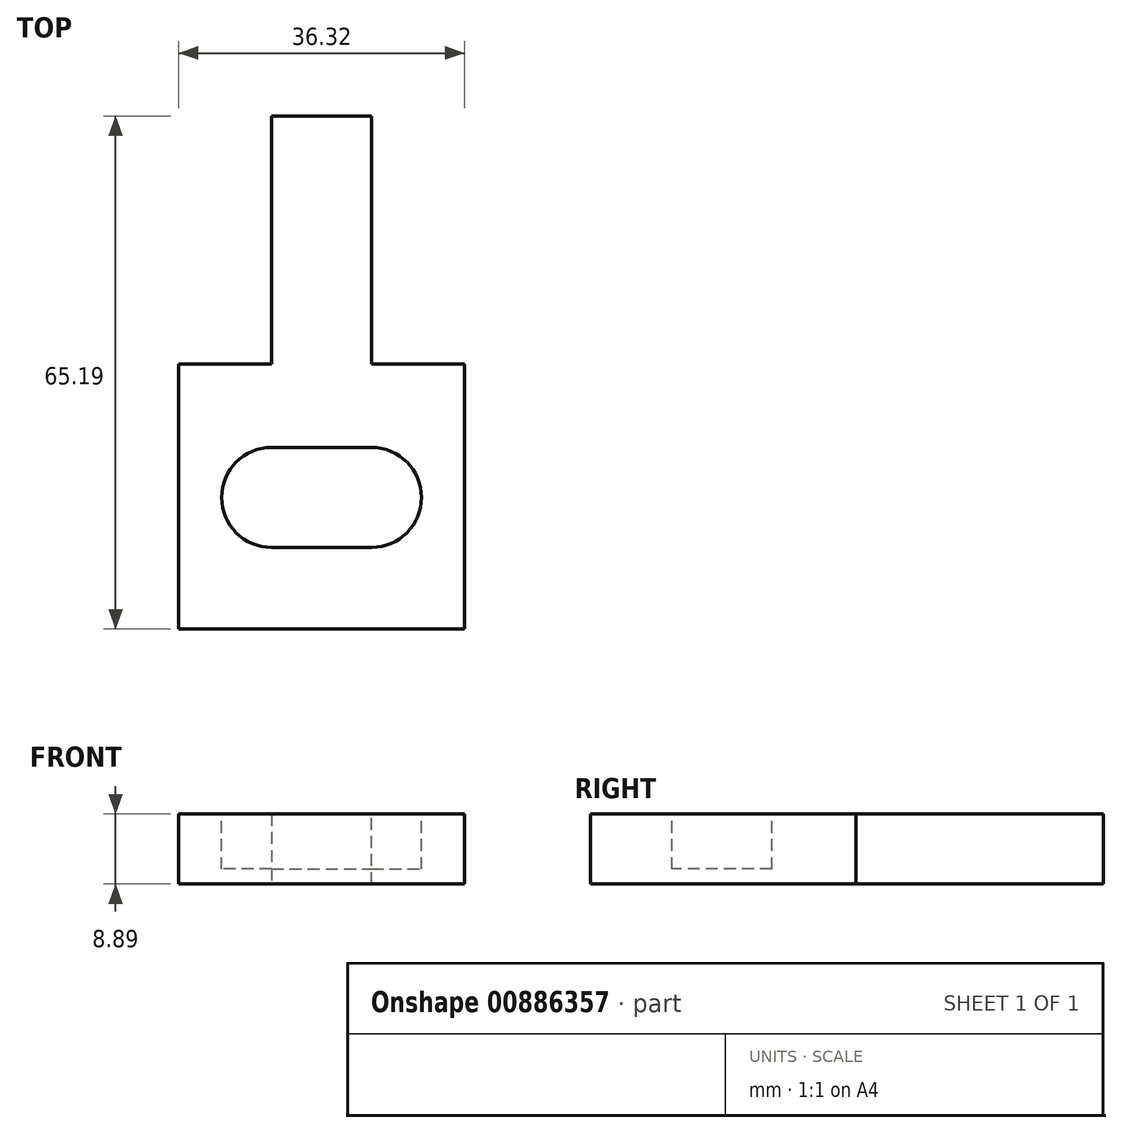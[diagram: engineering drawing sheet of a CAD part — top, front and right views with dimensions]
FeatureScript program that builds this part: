
annotation { "Feature Type Name" : "Feature", "Feature Type Description" : "" }
export const myFeature = defineFeature(function(context is Context, id is Id, definition is map)
    precondition{}
    {
        {
            var Q0;
            Q0=qCreatedBy(makeId("Top.planeOp"),FACE);
            var sketch = newSketch(context, id + "F0", { "sketchPlane" : qUnion([Q0])});
            skLineSegment(sketch, "E0.bottom", {"start": v(0, 0) * mm, "end": v(36.32, 0) * mm});
            skLineSegment(sketch, "E0.top", {"start": v(0, -46.14) * mm, "end": v(36.32, -46.14) * mm});
            skLineSegment(sketch, "E0.left", {"start": v(0, 0) * mm, "end": v(0, -46.14) * mm});
            skLineSegment(sketch, "E0.right", {"start": v(36.32, 0) * mm, "end": v(36.32, -46.14) * mm});
            skSolve(sketch);
        }
        {
            var Q0;
            Q0=makeQuery(id+"F0.imprint","IMPRINT",FACE,{"disambiguationData":[TD([[makeQuery(id+"F0.imprint","IMPRINT",EDGE,{"derivedFrom":sQuery(id+"F0.wireOp",EDGE,"E0.bottom")}),-1.0]])]});
            extrude(context, id + "F1", {"entities" : qUnion([Q0]), "depth" : 8.9 * mm, "offsetDistance" : 25.4 * mm});
        }
        {
            var Q0;
            Q0=makeQuery(id+"F1.opExtrude","CAP_FACE",FACE,{"disambiguationData":[OSD([sQuery(id+"F0.wireOp",EDGE,"E0.bottom"),sQuery(id+"F0.wireOp",EDGE,"E0.top"),sQuery(id+"F0.wireOp",EDGE,"E0.left"),sQuery(id+"F0.wireOp",EDGE,"E0.right")])],"isStart":false});
            var sketch = newSketch(context, id + "F2", { "sketchPlane" : qUnion([Q0])});
            skLineSegment(sketch, "E1", {"start": v(36.32, -46.14) * mm, "end": v(0, -46.14) * mm});
            skLineSegment(sketch, "E2", {"start": v(37, 0) * mm, "end": v(36.32, 0) * mm});
            skArc(sketch, "E3", {"start": v(24.5, -29.42) * mm, "mid": v(30.85, -23.07) * mm, "end": v(24.5, -16.72) * mm});
            skArc(sketch, "E4", {"start": v(11.81, -16.72) * mm, "mid": v(5.47, -23.07) * mm, "end": v(11.81, -29.42) * mm});
            skPoint(sketch, "E5.start.orphan", {"position": v(18.16, -23.07) * mm});
            skLineSegment(sketch, "E6.top", {"start": v(11.81, -29.42) * mm, "end": v(24.5, -29.42) * mm});
            skLineSegment(sketch, "E7.top", {"start": v(11.81, -16.72) * mm, "end": v(24.5, -16.72) * mm});
            skSolve(sketch);
        }
        {
            var Q0;
            Q0=makeQuery(id+"F2.imprint","IMPRINT",FACE,{"disambiguationData":[TD([[makeQuery(id+"F2.imprint","IMPRINT",EDGE,{"derivedFrom":sQuery(id+"F2.wireOp",EDGE,"E3")}),1.0]])]});
            extrude(context, id + "F3", {"entities" : qUnion([Q0]), "operationType" : NewBodyOperationType.REMOVE, "oppositeDirection" : true, "depth" : 7 * mm, "offsetDistance" : 25.4 * mm});
        }
        {
            var Q0;
            Q0=makeQuery(id+"F1.opExtrude","SWEPT_FACE",FACE,{"disambiguationData":[OSD([sQuery(id+"F0.wireOp",EDGE,"E0.bottom")])]});
            var sketch = newSketch(context, id + "F4", { "sketchPlane" : qUnion([Q0])});
            skLineSegment(sketch, "E8", {"start": v(0, 0) * mm, "end": v(0, 8.9) * mm});
            skLineSegment(sketch, "E9.right", {"start": v(-11.82, 4.45) * mm, "end": v(-11.82, 8.9) * mm});
            skLineSegment(sketch, "E10.right", {"start": v(-24.52, 4.45) * mm, "end": v(-24.52, 8.9) * mm});
            skLineSegment(sketch, "E11.top", {"start": v(-24.52, 0) * mm, "end": v(-11.82, 0) * mm});
            skLineSegment(sketch, "E11.left", {"start": v(-24.52, 4.45) * mm, "end": v(-24.52, 0) * mm});
            skLineSegment(sketch, "E11.right", {"start": v(-11.82, 4.45) * mm, "end": v(-11.82, 0) * mm});
            skPoint(sketch, "E12.orphan", {"position": v(-18.16, 4.45) * mm});
            skPoint(sketch, "E13.trimOffspring.end.orphan", {"position": v(-36.32, 0) * mm});
            skLineSegment(sketch, "E14.bottom", {"start": v(-24.52, 8.9) * mm, "end": v(-11.82, 8.9) * mm});
            skLineSegment(sketch, "E14.left", {"start": v(-24.52, 8.9) * mm, "end": v(-24.52, 0) * mm});
            skLineSegment(sketch, "E14.right", {"start": v(-11.82, 8.9) * mm, "end": v(-11.82, 0) * mm});
            skSolve(sketch);
        }
        {
            var Q0;
            Q0=makeQuery(id+"F4.imprint","IMPRINT",FACE,{"disambiguationData":[TD([[makeQuery(id+"F4.imprint","IMPRINT",EDGE,{"derivedFrom":sQuery(id+"F4.wireOp",EDGE,"E14.bottom")}),1.0]])]});
            extrude(context, id + "F5", {"entities" : qUnion([Q0]), "operationType" : NewBodyOperationType.ADD, "depth" : 25.4 * mm, "offsetDistance" : 25.4 * mm});
        }
        {
            var Q0;
            Q0=makeQuery(id+"F1.opExtrude","SWEPT_FACE",FACE,{"disambiguationData":[OSD([sQuery(id+"F0.wireOp",EDGE,"E0.top")])]});
            extrude(context, id + "F6", {"entities" : qUnion([Q0]), "operationType" : NewBodyOperationType.REMOVE, "oppositeDirection" : true, "depth" : 6.35 * mm, "offsetDistance" : 25.4 * mm});
        }
        {
            var Q0;
            {var subQ0=sQuery(id+"F0.wireOp",EDGE,"E0.left");var subQ3=sQuery(id+"F0.wireOp",EDGE,"E0.bottom");Q0=makeQuery(id+"F5.boolean.opBoolean","SPLIT",FACE,{"disambiguationData":[TD([makeQuery(id+"F1.opExtrude","SWEPT_FACE",FACE,{"disambiguationData":[OSD([subQ0])]})])],"derivedFrom":makeQuery(id+"F1.opExtrude","SWEPT_FACE",FACE,{"disambiguationData":[OSD([subQ3])]})});}
            var Q1;
            {var subQ0=sQuery(id+"F0.wireOp",EDGE,"E0.right");var subQ3=sQuery(id+"F0.wireOp",EDGE,"E0.bottom");Q1=makeQuery(id+"F5.boolean.opBoolean","SPLIT",FACE,{"disambiguationData":[TD([makeQuery(id+"F1.opExtrude","SWEPT_FACE",FACE,{"disambiguationData":[OSD([subQ0])]})])],"derivedFrom":makeQuery(id+"F1.opExtrude","SWEPT_FACE",FACE,{"disambiguationData":[OSD([subQ3])]})});}
            extrude(context, id + "F7", {"entities" : qUnion([Q0, Q1]), "operationType" : NewBodyOperationType.REMOVE, "oppositeDirection" : true, "depth" : 6.1 * mm, "offsetDistance" : 25.4 * mm});
        }
    });
